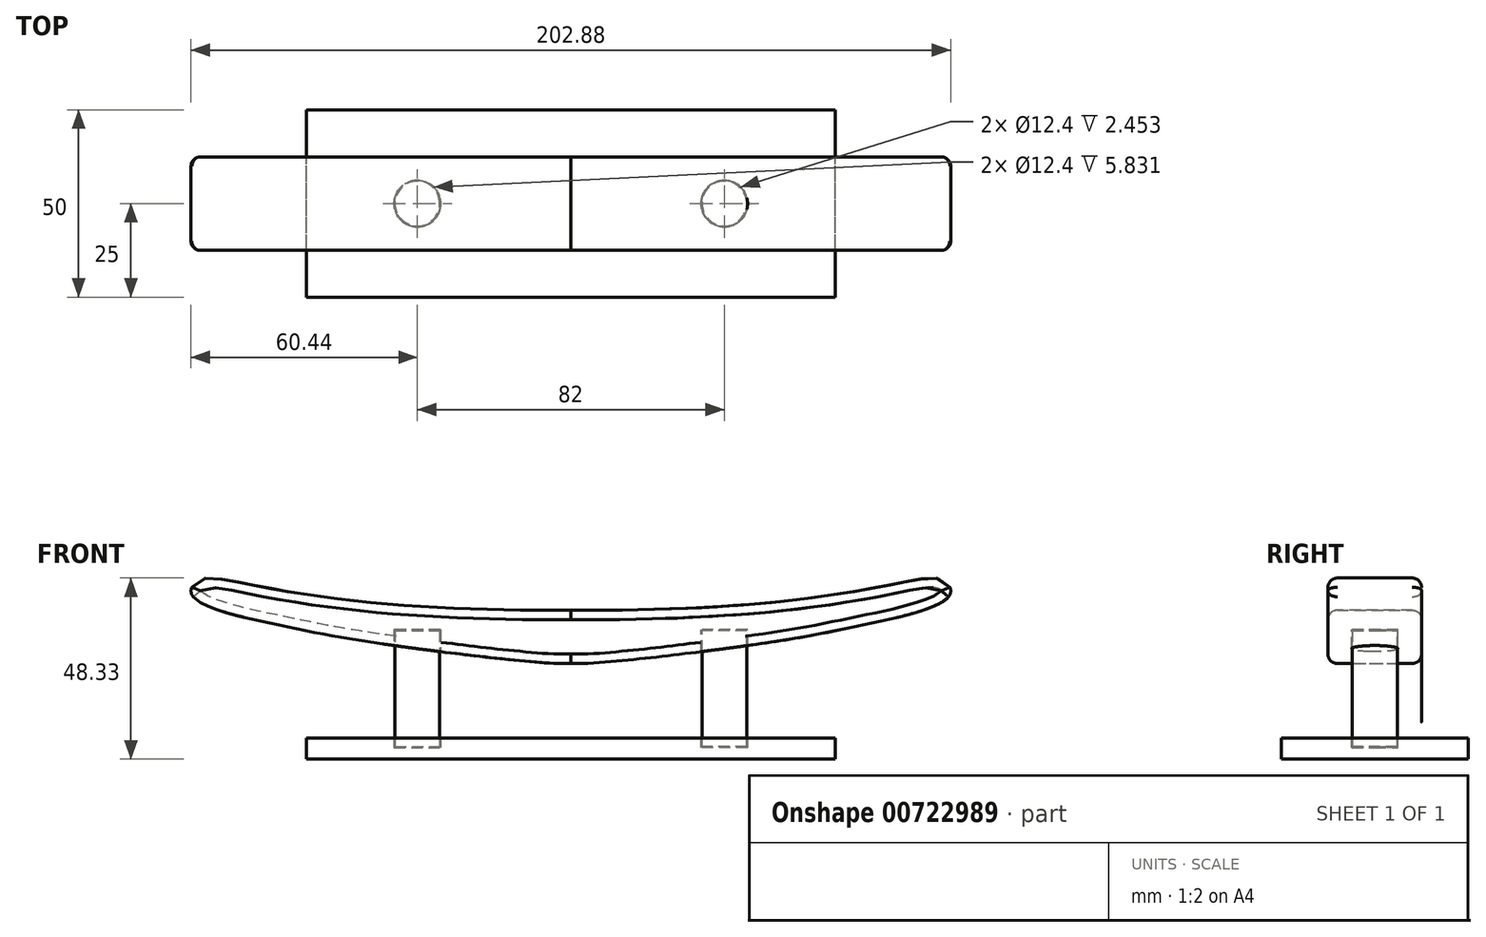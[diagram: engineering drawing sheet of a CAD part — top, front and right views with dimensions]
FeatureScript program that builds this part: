
annotation { "Feature Type Name" : "Feature", "Feature Type Description" : "" }
export const myFeature = defineFeature(function(context is Context, id is Id, definition is map)
    precondition{}
    {
        {
            var Q0;
            Q0=qCreatedBy(makeId("Front.planeOp"),FACE);
            var sketch = newSketch(context, id + "F0", { "sketchPlane" : qUnion([Q0])});
            skFitSpline(sketch, "E0", {"points": [v(0, 22.16) * mm, v(-100, 29.83) * mm, v(-101.06, 26.02) * mm, v(-77.06, 18.02) * mm, v(-53.06, 13.57) * mm, v(-5.29, 8.02) * mm, v(0, 7.95) * mm], "startDerivative": vector(-730.8, -5.5) * mm, "endDerivative": vector(32.9, -0.95) * mm});
            skLineSegment(sketch, "E1.right", {"start": v(-35, 16.72) * mm, "end": v(-35, -14.3) * mm});
            skLineSegment(sketch, "E2", {"start": v(-47, 16.72) * mm, "end": v(-47, -14.3) * mm});
            skLineSegment(sketch, "E3.bottom", {"start": v(-70.58, -12.05) * mm, "end": v(0, -12.05) * mm});
            skLineSegment(sketch, "E3.top", {"start": v(-70.58, -17.57) * mm, "end": v(0, -17.57) * mm});
            skLineSegment(sketch, "E3.left", {"start": v(-70.58, -12.05) * mm, "end": v(-70.58, -17.57) * mm});
            skLineSegment(sketch, "E4.MirrorCS", {"start": v(70.58, -12.05) * mm, "end": v(70.58, -17.57) * mm});
            skLineSegment(sketch, "E5.MirrorCS", {"start": v(70.58, -17.57) * mm, "end": v(0, -17.57) * mm});
            skLineSegment(sketch, "E6.MirrorCS", {"start": v(70.58, -12.05) * mm, "end": v(0, -12.05) * mm});
            skLineSegment(sketch, "E7.MirrorCS", {"start": v(47, 16.72) * mm, "end": v(47, -14.3) * mm});
            skLineSegment(sketch, "E8.MirrorCS", {"start": v(35, 16.72) * mm, "end": v(35, -14.3) * mm});
            skFitSpline(sketch, "E9.MirrorCS", {"points": [v(0, 22.16) * mm, v(100, 29.83) * mm, v(101.06, 26.02) * mm, v(77.06, 18.02) * mm, v(53.06, 13.57) * mm, v(5.29, 8.02) * mm, v(0, 7.95) * mm], "startDerivative": vector(730.8, -5.5) * mm, "endDerivative": vector(-32.9, -0.95) * mm});
            skLineSegment(sketch, "E10", {"start": v(-41, 17.56) * mm, "end": v(-41, -15.2) * mm});
            skLineSegment(sketch, "E11.MirrorCS", {"start": v(41, 17.56) * mm, "end": v(41, -15.2) * mm});
            skLineSegment(sketch, "E12", {"start": v(-47, 16.72) * mm, "end": v(-35, 16.72) * mm});
            skLineSegment(sketch, "E13", {"start": v(-35, -14.3) * mm, "end": v(-47, -14.3) * mm});
            skLineSegment(sketch, "E14", {"start": v(35, -14.3) * mm, "end": v(47, -14.3) * mm});
            skLineSegment(sketch, "E15", {"start": v(35, 16.72) * mm, "end": v(47, 16.72) * mm});
            skSolve(sketch);
        }
        {
            var Q0;
            {var subQ0=sQuery(id+"F0.wireOp",EDGE,"E9.MirrorCS");var subQ1=sQuery(id+"F0.wireOp",EDGE,"E0");var subQ2=makeQuery(id+"F0.imprint","INTERSECT",VERTEX,{"disambiguationData":[OD(0.0)],"derivedFrom":[subQ1,subQ0]});Q0=makeQuery(id+"F0.imprint","IMPRINT",FACE,{"disambiguationData":[TD([[makeQuery(id+"F0.imprint","IMPRINT",EDGE,{"disambiguationData":[TD([[subQ2,-1.0]])],"derivedFrom":subQ1}),1.0]])]});}
            var Q1;
            {var subQ0=sQuery(id+"F0.wireOp",EDGE,"E10");var subQ1=sQuery(id+"F0.wireOp",EDGE,"E0");var subQ2=makeQuery(id+"F0.imprint","INTERSECT",VERTEX,{"derivedFrom":[subQ1,subQ0]});Q1=makeQuery(id+"F0.imprint","IMPRINT",FACE,{"disambiguationData":[TD([[makeQuery(id+"F0.imprint","IMPRINT",EDGE,{"disambiguationData":[TD([[subQ2,-1.0]])],"derivedFrom":subQ1}),1.0]])]});}
            var Q2;
            {var subQ0=sQuery(id+"F0.wireOp",EDGE,"E2");var subQ1=sQuery(id+"F0.wireOp",EDGE,"E0");var subQ2=makeQuery(id+"F0.imprint","INTERSECT",VERTEX,{"derivedFrom":[subQ1,subQ0]});Q2=makeQuery(id+"F0.imprint","IMPRINT",FACE,{"disambiguationData":[TD([[makeQuery(id+"F0.imprint","IMPRINT",EDGE,{"disambiguationData":[TD([[subQ2,-1.0]])],"derivedFrom":subQ1}),1.0]])]});}
            var Q3;
            {var subQ0=sQuery(id+"F0.wireOp",EDGE,"E15");var subQ1=sQuery(id+"F0.wireOp",EDGE,"E7.MirrorCS");var subQ2=makeQuery(id+"F0.imprint","INTERSECT",VERTEX,{"derivedFrom":[subQ1,subQ0]});Q3=makeQuery(id+"F0.imprint","IMPRINT",FACE,{"disambiguationData":[TD([[makeQuery(id+"F0.imprint","IMPRINT",EDGE,{"disambiguationData":[TD([[subQ2,-1.0]])],"derivedFrom":subQ1}),-1.0]])]});}
            var Q4;
            {var subQ0=sQuery(id+"F0.wireOp",EDGE,"E15");var subQ1=sQuery(id+"F0.wireOp",EDGE,"E8.MirrorCS");var subQ2=makeQuery(id+"F0.imprint","INTERSECT",VERTEX,{"derivedFrom":[subQ1,subQ0]});Q4=makeQuery(id+"F0.imprint","IMPRINT",FACE,{"disambiguationData":[TD([[makeQuery(id+"F0.imprint","IMPRINT",EDGE,{"disambiguationData":[TD([[subQ2,-1.0]])],"derivedFrom":subQ1}),1.0]])]});}
            extrude(context, id + "F1", {"entities" : qUnion([Q0, Q1, Q2, Q3, Q4]), "endBound" : BoundingType.SYMMETRIC, "depth" : 25 * mm, "offsetDistance" : 25 * mm});
        }
        {
            var Q0;
            {var subQ0=sQuery(id+"F0.wireOp",EDGE,"E2");Q0=makeQuery(id+"F0.imprint","IMPRINT",FACE,{"disambiguationData":[TD([[makeQuery(id+"F0.imprint","IMPRINT",EDGE,{"derivedFrom":subQ0}),1.0]])]});}
            var Q1;
            Q1=sQuery(id+"F0.wireOp",EDGE,"E10");
            revolve(context, id + "F2", {"surfaceOperationType" : NewSurfaceOperationType.NEW, "entities" : qUnion([Q0]), "axis" : qUnion([Q1]), "revolveType" : RevolveType.FULL, "oppositeDirection" : true});
        }
        {
            var Q0;
            {var subQ0=sQuery(id+"F0.wireOp",EDGE,"E7.MirrorCS");Q0=makeQuery(id+"F0.imprint","IMPRINT",FACE,{"disambiguationData":[TD([[makeQuery(id+"F0.imprint","IMPRINT",EDGE,{"derivedFrom":subQ0}),-1.0]])]});}
            var Q1;
            Q1=sQuery(id+"F0.wireOp",EDGE,"E11.MirrorCS");
            revolve(context, id + "F3", {"surfaceOperationType" : NewSurfaceOperationType.NEW, "entities" : qUnion([Q0]), "axis" : qUnion([Q1]), "revolveType" : RevolveType.FULL});
        }
        {
            var Q0;
            Q0=makeQuery(id+"F0.imprint","IMPRINT",FACE,{"disambiguationData":[TD([[makeQuery(id+"F0.imprint","IMPRINT",EDGE,{"derivedFrom":sQuery(id+"F0.wireOp",EDGE,"E3.top")}),1.0]])]});
            var Q1;
            {var subQ0=sQuery(id+"F0.wireOp",EDGE,"E11.MirrorCS");var subQ1=sQuery(id+"F0.wireOp",EDGE,"E6.MirrorCS");var subQ2=makeQuery(id+"F0.imprint","INTERSECT",VERTEX,{"derivedFrom":[subQ1,subQ0]});Q1=makeQuery(id+"F0.imprint","IMPRINT",FACE,{"disambiguationData":[TD([[makeQuery(id+"F0.imprint","IMPRINT",EDGE,{"disambiguationData":[TD([[subQ2,-1.0]])],"derivedFrom":subQ1}),1.0]])]});}
            var Q2;
            {var subQ0=sQuery(id+"F0.wireOp",EDGE,"E7.MirrorCS");var subQ1=sQuery(id+"F0.wireOp",EDGE,"E6.MirrorCS");var subQ2=makeQuery(id+"F0.imprint","INTERSECT",VERTEX,{"derivedFrom":[subQ1,subQ0]});Q2=makeQuery(id+"F0.imprint","IMPRINT",FACE,{"disambiguationData":[TD([[makeQuery(id+"F0.imprint","IMPRINT",EDGE,{"disambiguationData":[TD([[subQ2,-1.0]])],"derivedFrom":subQ1}),1.0]])]});}
            var Q3;
            {var subQ0=sQuery(id+"F0.wireOp",EDGE,"E13");var subQ1=sQuery(id+"F0.wireOp",EDGE,"E1.right");var subQ2=makeQuery(id+"F0.imprint","INTERSECT",VERTEX,{"derivedFrom":[subQ1,subQ0]});Q3=makeQuery(id+"F0.imprint","IMPRINT",FACE,{"disambiguationData":[TD([[makeQuery(id+"F0.imprint","IMPRINT",EDGE,{"disambiguationData":[TD([[subQ2,1.0]])],"derivedFrom":subQ1}),-1.0]])]});}
            var Q4;
            {var subQ0=sQuery(id+"F0.wireOp",EDGE,"E13");var subQ1=sQuery(id+"F0.wireOp",EDGE,"E2");var subQ2=makeQuery(id+"F0.imprint","INTERSECT",VERTEX,{"derivedFrom":[subQ1,subQ0]});Q4=makeQuery(id+"F0.imprint","IMPRINT",FACE,{"disambiguationData":[TD([[makeQuery(id+"F0.imprint","IMPRINT",EDGE,{"disambiguationData":[TD([[subQ2,1.0]])],"derivedFrom":subQ1}),1.0]])]});}
            extrude(context, id + "F4", {"entities" : qUnion([Q0, Q1, Q2, Q3, Q4]), "endBound" : BoundingType.SYMMETRIC, "depth" : 50 * mm, "offsetDistance" : 25 * mm});
        }
        {
            var Q0;
            Q0=makeQuery(id+"F1.opExtrude","CAP_FACE",FACE,{"disambiguationData":[OSD([sQuery(id+"F0.wireOp",EDGE,"E0"),sQuery(id+"F0.wireOp",EDGE,"E9.MirrorCS")])],"isStart":false});
            var Q1;
            Q1=makeQuery(id+"F1.opExtrude","CAP_FACE",FACE,{"disambiguationData":[OSD([sQuery(id+"F0.wireOp",EDGE,"E0"),sQuery(id+"F0.wireOp",EDGE,"E9.MirrorCS")])],"isStart":true});
            fillet(context, id + "F5", {"entities" : qUnion([Q0, Q1]), "radius" : 2.5 * mm, "allowEdgeOverflow" : false});
        }
        {
            var Q0;
            Q0=makeQuery(id+"F2.opRevolve","SWEPT_BODY",BODY,{"disambiguationData":[OSD([sQuery(id+"F0.wireOp",EDGE,"E2"),sQuery(id+"F0.wireOp",EDGE,"E10"),sQuery(id+"F0.wireOp",EDGE,"E12"),sQuery(id+"F0.wireOp",EDGE,"E13")])]});
            var Q1;
            Q1=makeQuery(id+"F3.opRevolve","SWEPT_BODY",BODY,{"disambiguationData":[OSD([sQuery(id+"F0.wireOp",EDGE,"E7.MirrorCS"),sQuery(id+"F0.wireOp",EDGE,"E11.MirrorCS"),sQuery(id+"F0.wireOp",EDGE,"E14"),sQuery(id+"F0.wireOp",EDGE,"E15")])]});
            var Q2;
            Q2=makeQuery(id+"F1.opExtrude","SWEPT_BODY",BODY,{"disambiguationData":[OSD([sQuery(id+"F0.wireOp",EDGE,"E0"),sQuery(id+"F0.wireOp",EDGE,"E9.MirrorCS")])]});
            var Q3;
            Q3=makeQuery(id+"F4.opExtrude","SWEPT_BODY",BODY,{"disambiguationData":[OSD([sQuery(id+"F0.wireOp",EDGE,"E3.bottom"),sQuery(id+"F0.wireOp",EDGE,"E3.top"),sQuery(id+"F0.wireOp",EDGE,"E3.left"),sQuery(id+"F0.wireOp",EDGE,"E4.MirrorCS"),sQuery(id+"F0.wireOp",EDGE,"E5.MirrorCS"),sQuery(id+"F0.wireOp",EDGE,"E6.MirrorCS")])]});
            booleanBodies(context, id + "F6", {"operationType" : BooleanOperationType.SUBTRACTION, "tools" : qUnion([Q0, Q1]), "targets" : qUnion([Q2, Q3]), "offset" : true, "offsetAll" : true, "offsetDistance" : 0.2 * mm, "keepTools" : true});
        }
    });
